AUTODESK INVENTOR PART (.ipt)
format: ipt  version: 2015 (Build 190159000, 159)  size: 122,368 bytes
history: native  units: mm
features: other x1, extrude x1, sketch x1
ambient origin geometry x8: Origin, YZ Plane, XZ Plane, XY Plane, X Axis, Y Axis, Z Axis, Center Point
bodies: Solid1 (feature_tree)
feature tree (3):
  other  "DimensionalCalibration"
  extrude  "Extrusion1"  Depth=40.0mm
  sketch  "Sketch1"  dims[d0=60.0mm d1=40.0mm d2=8.85825mm d3=8.0645mm d4=8.0mm d5=10.0mm d6=3.7973mm d7=5.1054mm d8=3.2639mm d9=3.7973mm d21=10.0mm d22=0.0mm d23=9.312082mm d24=10.228626mm]
